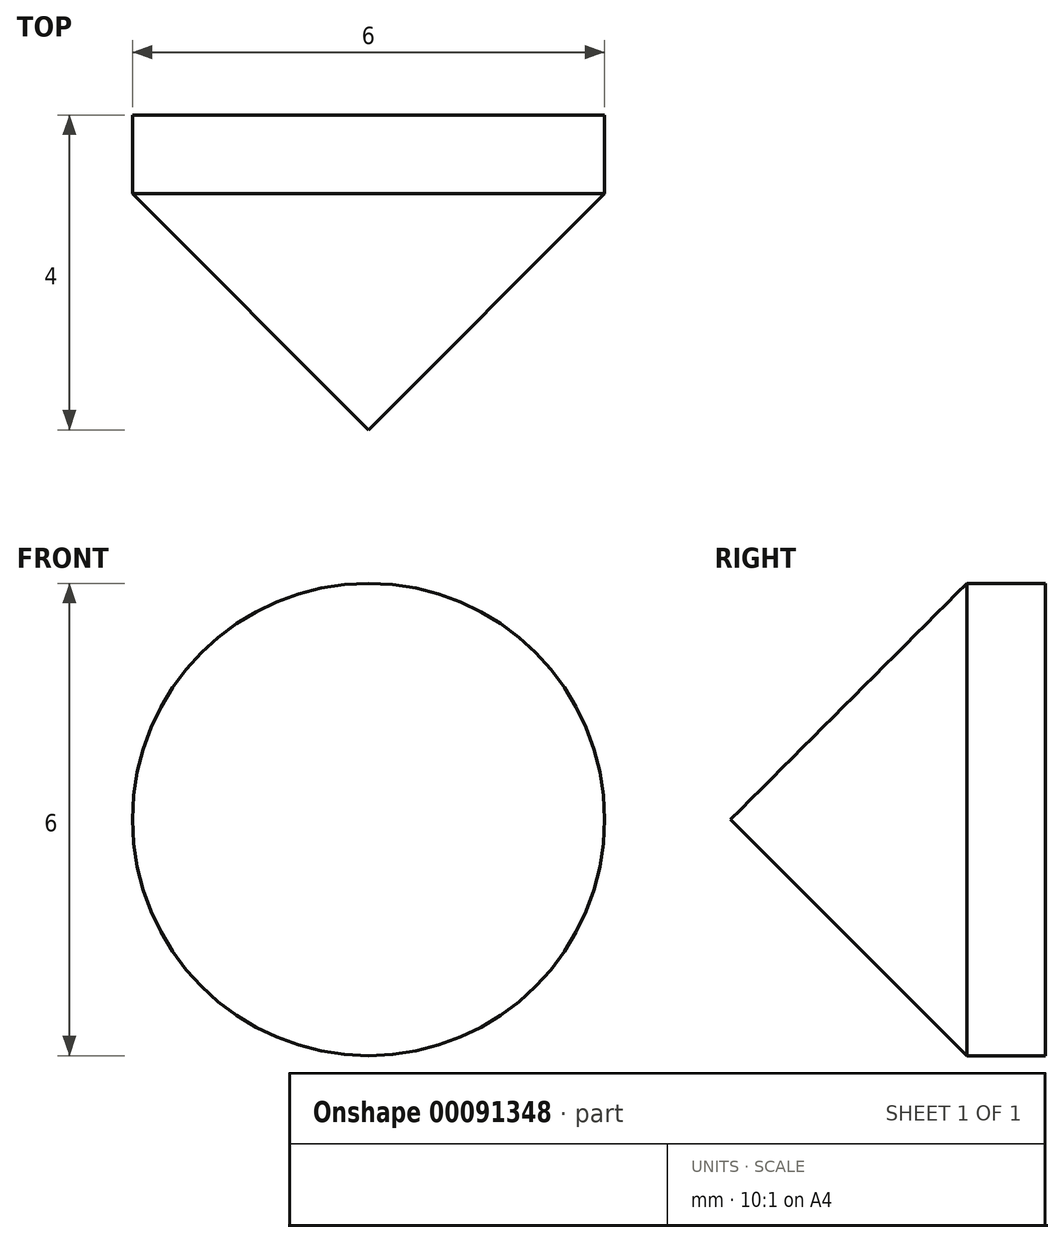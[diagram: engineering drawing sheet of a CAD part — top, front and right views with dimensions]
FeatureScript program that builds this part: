
annotation { "Feature Type Name" : "Feature", "Feature Type Description" : "" }
export const myFeature = defineFeature(function(context is Context, id is Id, definition is map)
    precondition{}
    {
        {
            var Q0;
            Q0=qCreatedBy(makeId("Front.planeOp"),FACE);
            var sketch = newSketch(context, id + "F0", { "sketchPlane" : qUnion([Q0])});
            skCircle(sketch, "E0", {"center": v(0, 0) * mm, "radius": 3 * mm});
            skSolve(sketch);
        }
        {
            var Q0;
            Q0=makeQuery(id+"F0.imprint","IMPRINT",FACE,{"disambiguationData":[TD([[makeQuery(id+"F0.imprint","IMPRINT",EDGE,{"derivedFrom":sQuery(id+"F0.wireOp",EDGE,"E0")}),1.0]])]});
            extrude(context, id + "F1", {"entities" : qUnion([Q0]), "oppositeDirection" : true, "depth" : 4 * mm});
        }
        {
            var Q0;
            Q0=makeQuery(id+"F1.opExtrude","CAP_EDGE",EDGE,{"disambiguationData":[OSD([sQuery(id+"F0.wireOp",EDGE,"E0")])],"isStart":true});
            chamfer(context, id + "F2", {"entities" : qUnion([Q0]), "width" : 3 * mm});
        }
    });
